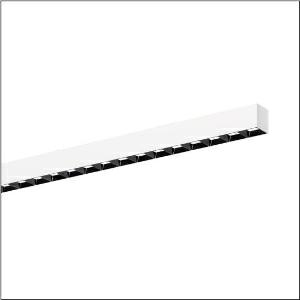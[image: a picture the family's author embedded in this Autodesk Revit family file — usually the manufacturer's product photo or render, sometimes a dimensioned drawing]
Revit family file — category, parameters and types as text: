
# Revit family: silica_r__21_51mx21tbt5w_e527
name_source: partatom
category: Lighting Fixtures
units: mm (PartAtom-declared; Revit-internal decimal feet)

## family parameters
Cut with Voids When Loaded = No
Host = Face
Light Source = No
Part Type = Normal
Room Calculation Point = No
Round Connector Dimension = Use Diameter
Shared = No

## types (1)
- --- (1 x LED, 4650 lm, 40.3 W, 6500K)
    Apparent Load = 40 VA
    CIE Flux Codes = 85 99 100 100 100
    Color Rendering = 80
    Color Temperature = 6500K
    Default Elevation = 1800 mm
    Description = Silica® 21, office luminaire, primary light control with darklight reflector, of PMMA, black, CAT 2 (L<= 3000cd/m²), light emission: direct distribution, primary light characteristic: symmetric, installation type: surface-mounted, LED, rated luminous flux: 4.650lm, luminous efficacy: 110lm/W, light colour: 8tw, colour temperature: 2700..6500K, control gear: ECG DALI, with terminal, 3+2-pole, max. 2.5mm², mains connection: 220..240V, AC, 50/60Hz, rated input power: 42.3W, luminaire housing, of aluminium, traffic white (RAL 9016), length: 1.504mm, width: 53mm, height: 53mm, protection rating (complete): IP20, insulation class (complete): insulation class I (protective earthing), certification: CE, permissible operating ambient temperature: 0..+35°C, standard: EN 50419, packaging unit: 1 piece
    Height = 0 mm  [stored 0 ft]
    Lamp = 1 x LED
    Lamp Light Flux = 4650 lm
    Lamp Power = 40.3 W
    Lamp count = 1
    Length = 1504 mm
    Luminous efficacy = 115 lm/W
    Manufacturer = Siteco
    ModVariant = No
    Model = 51MX21TBT5W
    Mounting Place = Ceiling
    Mounting Type = Recessed
    Number of Poles = 1
    OnlyDefault = Yes
    Power Factor = 1
    Product Name = Silica® 21
    Product group = office luminaire | ceiling recessed
    ProductGroupID = 401
    Protection Class = Protection class I
    Protection Degree = IP 20
    RLX_Detail_Level = 1
    RLX_Emergency_Light_Flux = 0 lm
    RLX_Emergency_Type = 0
    RLX_Emergency_Type_DB = No
    RlxData = <blob elided: 41365 chars, md5=37f0c11b>
    Socket = socket
    Standby Power = 0 W
    System Light Flux = 4650 lm
    System Power = 40 W
    Type Comments = individual setting
    Type Image = l_1313592.jpg
    URL = http://relux.com
    VarID = @adj_089451
    Voltage = 0 V
    Weight = 0.00 kg
    Width = 53 mm

note: [stored X ft] marks values corroborated as IEEE doubles in the binary element streams (Revit-internal decimal feet)

## geometry (parser evidence)
native form markers: Blend x4, Sweep x10
no freeform markers — native parametric forms only
